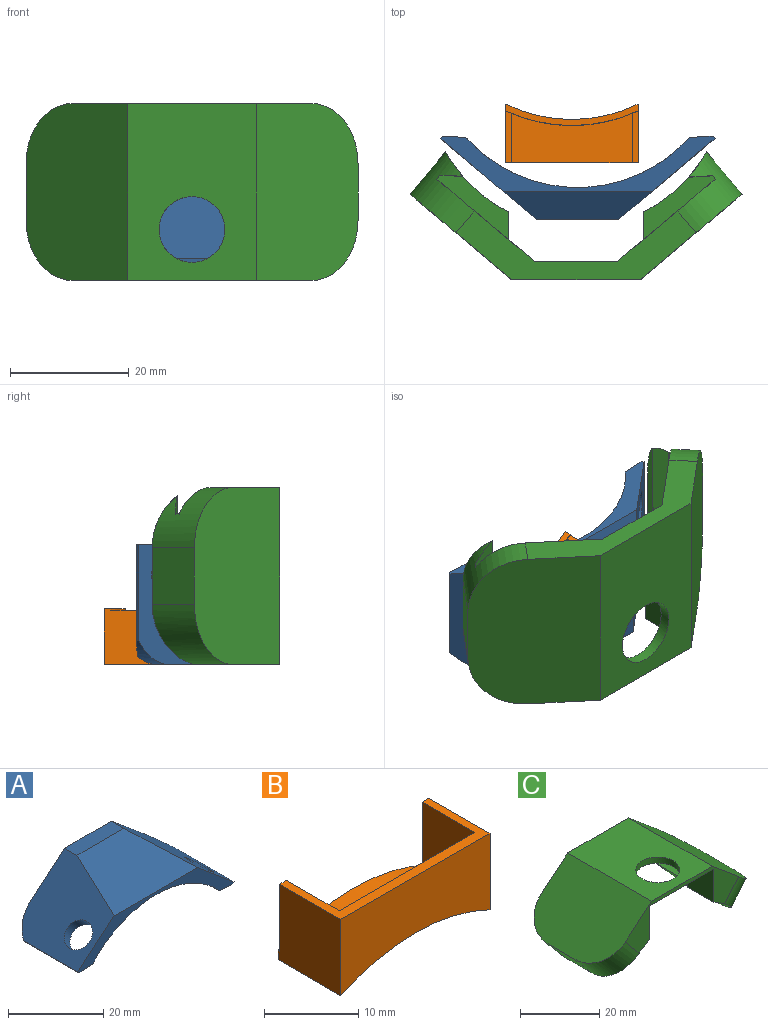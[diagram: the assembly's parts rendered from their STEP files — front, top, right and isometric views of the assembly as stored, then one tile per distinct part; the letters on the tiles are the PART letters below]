
ASSEMBLY  parts=3 mates=2
PART A: 40 faces, bbox 47.4x21.3x18 mm
  f0: torus R=15.15mm, axis (0,-1,0), area 22.5mm2, adj f1,f8,f11,f12
  f1: cylinder r=29.12mm len=5.11mm, axis (0,1,0), area 19.9mm2, adj f0,f9,f10,f20
  f2: bspline ~8.45x2.65mm, area 0.1mm2, adj f3,f37
  f3: plane 9.44x3.14mm, normal (-0.64,0,-0.77), area 6.4mm2, adj f2,f18,f37
  f4: plane 8.75x2.45mm, normal (-0.64,0,-0.77), area 6.4mm2, adj f15,f16,f18,f37
  f5: bspline ~8.68x3.45mm, area 0.1mm2, adj f6,f36
  f6: plane 9.44x3.14mm, normal (0.64,0,-0.77), area 6.4mm2, adj f5,f19,f36
  f7: plane 8.75x2.45mm, normal (0.64,0,-0.77), area 6.4mm2, adj f19,f21,f22,f36
  f8: bspline ~7.83x4.14mm, area 18.1mm2, adj f0,f9,f13,f28
  f9: cylinder r=5.08mm len=5.11mm, axis (0,1,0), area 22.2mm2, adj f1,f8,f20,f28
  f10: cylinder r=5.08mm len=5.11mm, axis (0,-1,0), area 22.2mm2, adj f1,f11,f20,f27
  f11: bspline ~9.36x4.49mm, area 18.1mm2, adj f0,f10,f14,f27
  f12: cone r=29.12mm half-angle=20.6deg, axis (0,1,0), area 46.9mm2, adj f0,f13,f14,f26
  f13: bspline ~10.91x6.7mm, area 23.3mm2, adj f8,f12,f25,f28
  f14: bspline ~9.02x6.04mm, area 23.3mm2, adj f11,f12,f24,f27
  f15: bspline ~8.01x3.09mm, area 0.8mm2, adj f4,f35,f37
  f16: bspline ~4.22x2.61mm, area 0.8mm2, adj f4,f35,f37
  f17: cylinder r=10.16mm len=8.09mm, axis (0.64,0,0.77), area 21.6mm2, adj f20,f33,f34,f35,f37
  f18: cylinder r=3.37mm len=6.87mm, axis (-0.64,0,-0.77), area 56.4mm2, adj f3,f4,f33,f37
  f19: cylinder r=3.37mm len=6.87mm, axis (0.64,0,-0.77), area 56.4mm2, adj f6,f7,f31,f36
  f20: plane 33.94x10.44mm, normal (0,1,0), area 112.9mm2, adj f1,f9,f10,f17,f23,f27,f28,f31
  f21: bspline ~8.01x3.09mm, area 0.8mm2, adj f7,f29,f36
  f22: bspline ~4.22x2.61mm, area 0.8mm2, adj f7,f29,f36
  f23: cylinder r=10.16mm len=8.09mm, axis (0.64,0,-0.77), area 21.6mm2, adj f20,f29,f30,f31,f36
  f24: bspline ~7.31x5.83mm, area 11.5mm2, adj f14,f26,f27,f38
  f25: bspline ~7.31x5.83mm, area 11.5mm2, adj f13,f26,f28,f38
  f26: torus R=39.28mm, axis (0,1,0), area 80.2mm2, adj f12,f24,f25,f38
  f27: cylinder r=13.97mm len=20.19mm, axis (0,1,0), area 93.4mm2, adj f10,f11,f14,f20,f24,f37,f38
  f28: cylinder r=13.97mm len=20.19mm, axis (0,1,0), area 93.4mm2, adj f8,f9,f13,f20,f25,f36,f38
  f29: plane 19.3x4.37mm, normal (0.06,0,-1), area 70mm2, adj f21,f22,f23,f30,f36,f38
  f30: plane 16.13x0.39mm, normal (-0.77,0,-0.64), area 8.2mm2, adj f23,f29,f31,f38
  f31: plane 20.19x16.23mm, normal (-0.64,0,0.77), area 323.6mm2, adj f19,f20,f23,f30,f32,f38,f39
  f32: plane 13.93x3.68mm, normal (0,0,1), area 51.3mm2, adj f20,f31,f33,f39
  f33: plane 20.19x16.23mm, normal (0.64,0,0.77), area 323.6mm2, adj f17,f18,f20,f32,f34,f38,f39
  f34: plane 16.13x0.39mm, normal (0.77,0,-0.64), area 8.2mm2, adj f17,f33,f35,f38
  f35: plane 19.3x4.37mm, normal (-0.06,0,-1), area 70mm2, adj f15,f16,f17,f34,f37,f38
  f36: cylinder r=25.31mm len=20.19mm, axis (0,1,0), area 150.7mm2, adj f5,f6,f7,f19,f20,f21,f22,f23
  f37: cylinder r=25.31mm len=20.19mm, axis (0,1,0), area 150.7mm2, adj f2,f3,f4,f15,f16,f17,f18,f20
  f38: plane 46.4x9.45mm, normal (0,-1,0), area 109.7mm2, adj f24,f25,f26,f27,f28,f29,f30,f31
  f39: plane 24.83x16.51mm, normal (0,-0.27,0.96), area 332mm2, adj f31,f32,f33,f38
PART B: 12 faces, bbox 22.4x9.4x9.9 mm
  f0: cylinder r=25.31mm len=22.35mm, axis (0,1,0), area 218.1mm2, adj f1,f7,f8,f11
  f1: plane 9.9x9.42mm, normal (1,0,0), area 91.1mm2, adj f0,f2,f8,f9,f10,f11
  f2: plane 8.78x1.02mm, normal (0,1,0), area 8.7mm2, adj f1,f3,f9,f10
  f3: plane 8.33x7.9mm, normal (-1,0,0), area 65.7mm2, adj f2,f4,f9,f10
  f4: plane 20.32x8.33mm, normal (0,1,0), area 141.3mm2, adj f3,f5,f9,f10
  f5: plane 8.33x7.9mm, normal (1,0,0), area 65.7mm2, adj f4,f6,f9,f10
  f6: plane 8.78x1.02mm, normal (0,1,0), area 8.7mm2, adj f5,f7,f9,f10
  f7: plane 9.9x9.42mm, normal (-1,0,0), area 91.1mm2, adj f0,f6,f8,f9,f10,f11
  f8: plane 22.35x9.9mm, normal (0,-1,0), area 182.2mm2, adj f0,f1,f7,f9
  f9: plane 22.35x9.17mm, normal (0,0,1), area 44.4mm2, adj f1,f2,f3,f4,f5,f6,f7,f8
  f10: cylinder r=26.33mm len=22.35mm, axis (0,1,0), area 170.6mm2, adj f1,f2,f3,f4,f5,f6,f7,f11
  f11: plane 22.35x3.62mm, normal (0,1,0), area 23.5mm2, adj f0,f1,f7,f10
PART C: 68 faces, bbox 57x30.9x22.6 mm
  f0: plane 5.64x1.52mm, normal (0,-1,0), area 7.6mm2, adj f2,f6,f8,f55,f57
  f1: plane 14.12x3.94mm, normal (0,0,-1), area 55.6mm2, adj f3,f19,f28,f59
  f2: plane 3.06x2.74mm, normal (0.64,0,-0.77), area 4.6mm2, adj f0,f15,f51,f57
  f3: plane 16.5x13.84mm, normal (0.64,0,-0.77), area 49mm2, adj f1,f17,f24,f28,f51,f57,f59
  f4: plane 3.06x2.74mm, normal (-0.64,0,-0.77), area 4.6mm2, adj f5,f7,f47,f58
  f5: cylinder r=10.29mm len=20.57mm, axis (-0.64,0,-0.77), area 223.3mm2, adj f4,f19,f20,f52,f53,f54,f58,f66
  f6: plane 7.9x0.7mm, normal (-1,0,0), area 5.5mm2, adj f0,f11,f55,f56
  f7: plane 5.64x1.52mm, normal (0,-1,0), area 7.6mm2, adj f4,f9,f10,f55,f58
  f8: plane 10.28x9.42mm, normal (1,0,0), area 96.9mm2, adj f0,f12,f14,f15,f55
  f9: plane 10.28x9.42mm, normal (-1,0,0), area 96.9mm2, adj f7,f13,f14,f47,f55
  f10: plane 7.9x0.7mm, normal (1,0,0), area 5.5mm2, adj f7,f11,f55,f56
  f11: plane 19.81x0.7mm, normal (0,-1,0), area 13.8mm2, adj f6,f10,f55,f56
  f12: cylinder r=25.31mm len=28.4mm, axis (0,1,0), area 145.3mm2, adj f8,f14,f15,f22,f23,f24,f27,f32
  f13: cylinder r=25.31mm len=28.49mm, axis (0,1,0), area 147.8mm2, adj f9,f14,f21,f25,f26,f34,f35,f36
  f14: plane 40.47x13.84mm, normal (0,-1,0), area 156.8mm2, adj f8,f9,f12,f13,f29,f30,f31,f45
  f15: plane 12.12x10.86mm, normal (0,1,0), area 41.5mm2, adj f2,f8,f12,f17,f18,f22,f49
  f16: plane 16.03x0.57mm, normal (-0.77,0,0.64), area 12mm2, adj f19,f20,f21,f25,f47,f54
  f17: plane 16.03x0.68mm, normal (0.77,0,0.64), area 14.3mm2, adj f3,f15,f18,f22,f24,f50
  f18: plane 5.26x3.69mm, normal (0.64,0,-0.77), area 9.6mm2, adj f15,f17,f51
  f19: plane 16.5x13.84mm, normal (-0.64,0,-0.77), area 49mm2, adj f1,f5,f16,f25,f28,f58,f59
  f20: plane 5.26x3.69mm, normal (-0.64,0,-0.77), area 9.6mm2, adj f5,f16,f47
  f21: plane 19.81x4.82mm, normal (0.06,0,1), area 72mm2, adj f13,f16,f25,f36,f47
  f22: plane 19.5x4.4mm, normal (-0.06,0,1), area 68.5mm2, adj f12,f15,f17,f23,f24
  f23: bspline ~7.34x1.85mm, area 0mm2, adj f12,f22
  f24: cylinder r=10.16mm len=13.78mm, axis (0.64,0,-0.77), area 108.3mm2, adj f3,f12,f17,f22,f27,f28,f29
  f25: cylinder r=10.16mm len=13.78mm, axis (0.64,0,0.77), area 108.9mm2, adj f13,f16,f19,f21,f26,f28,f31
  f26: plane 9.55x7.14mm, normal (0.77,0,-0.64), area 89mm2, adj f13,f25,f31,f46
  f27: plane 9.55x7.14mm, normal (-0.77,0,-0.64), area 89mm2, adj f12,f24,f29,f45
  f28: plane 40.47x11.59mm, normal (0,1,0), area 178.9mm2, adj f1,f3,f19,f24,f25,f29,f30,f31
  f29: plane 29.87x17.19mm, normal (-0.64,0,0.77), area 626mm2, adj f14,f24,f27,f28,f30,f45
  f30: plane 29.87x21.65mm, normal (0,0,1), area 549.7mm2, adj f14,f28,f29,f31,f60
  f31: plane 29.87x17.19mm, normal (0.64,0,0.77), area 626mm2, adj f14,f25,f26,f28,f30,f46
  f32: plane 9.44x3.14mm, normal (0.64,0,-0.77), area 6.4mm2, adj f12,f40,f43
  f33: plane 9.44x3.14mm, normal (0.64,0,-0.77), area 6.4mm2, adj f12,f39,f43
  f34: plane 9.44x3.14mm, normal (-0.64,0,-0.77), area 6.4mm2, adj f13,f38,f41
  f35: plane 9.44x3.14mm, normal (-0.64,0,-0.77), area 6.4mm2, adj f13,f37,f41
  f36: bspline ~7.34x1.85mm, area 0mm2, adj f13,f21
  f37: bspline ~8.68x3.09mm, area 0.1mm2, adj f13,f35
  f38: bspline ~8.45x2.65mm, area 0.1mm2, adj f13,f34
  f39: bspline ~8.68x3.45mm, area 0.1mm2, adj f12,f33
  f40: bspline ~8.45x2.3mm, area 0.1mm2, adj f12,f32
  f41: cylinder r=3.37mm len=7.03mm, axis (-0.64,0,-0.77), area 61.8mm2, adj f13,f34,f35,f42
  f42: plane 6.73x5.16mm, normal (-0.64,0,-0.77), area 35.6mm2, adj f41
  f43: cylinder r=3.37mm len=7.03mm, axis (0.64,0,-0.77), area 61.8mm2, adj f12,f32,f33,f44
  f44: plane 6.73x5.16mm, normal (0.64,0,-0.77), area 35.6mm2, adj f43
  f45: cylinder r=10.16mm len=13.78mm, axis (-0.64,0,0.77), area 136.3mm2, adj f12,f14,f27,f29
  f46: cylinder r=10.16mm len=13.78mm, axis (-0.64,0,-0.77), area 136.3mm2, adj f13,f14,f26,f31
  f47: plane 12.12x10.75mm, normal (0,1,0), area 41.1mm2, adj f4,f9,f13,f16,f20,f21,f53
  f48: plane 20.72x15.91mm, normal (0.64,0,-0.77), area 332.4mm2, adj f51,f63,f64
  f49: plane 7.22x6.06mm, normal (-0.64,0,0.77), area 7.3mm2, adj f15,f51
  f50: plane 7.77x0.58mm, normal (-0.64,0,0.77), area 4mm2, adj f17,f51
  f51: cylinder r=10.29mm len=20.57mm, axis (0.64,0,-0.77), area 223.7mm2, adj f2,f3,f18,f48,f49,f50,f57,f61
  f52: plane 20.71x15.89mm, normal (-0.64,0,-0.77), area 332.2mm2, adj f5,f65,f66,f67
  f53: plane 7.22x6.06mm, normal (0.64,0,0.77), area 7.3mm2, adj f5,f47
  f54: plane 7.77x0.58mm, normal (0.64,0,0.77), area 4mm2, adj f5,f16
  f55: plane 22.86x9.42mm, normal (0,0,-1), area 58.9mm2, adj f0,f6,f7,f8,f9,f10,f11,f14
  f56: plane 24.41x19.81mm, normal (0,0,-1), area 386.6mm2, adj f6,f10,f11,f57,f58,f59,f60
  f57: plane 16.51x3.66mm, normal (1,0,0), area 33.4mm2, adj f0,f2,f3,f51,f56,f59,f61
  f58: plane 16.51x3.66mm, normal (-1,0,0), area 33.4mm2, adj f4,f5,f7,f19,f56,f59,f66
  f59: plane 19.81x3.66mm, normal (0,-1,0), area 32mm2, adj f1,f3,f19,f56,f57,f58
  f60: cylinder r=5.56mm len=11.11mm, axis (0,0,-1), area 65.2mm2, adj f30,f56
  f61: cylinder r=0.64mm len=3.43mm, axis (1,0,0), area 10.1mm2, adj f51,f57,f62
  f62: plane 0.54x0.31mm, normal (1,0,0), area 0mm2, adj f51,f61
  f63: plane 0.55x0.06mm, normal (1,0,0), area 0mm2, adj f48,f64
  f64: cylinder r=0.64mm len=0.55mm, axis (1,0,0), area 0mm2, adj f48,f63
  f65: plane 0.98x0.23mm, normal (-1,0,0), area 0.2mm2, adj f52,f66,f67
  f66: cylinder r=0.64mm len=3.63mm, axis (-1,0,0), area 10.5mm2, adj f5,f52,f58,f65,f67
  f67: cylinder r=0.64mm len=0.49mm, axis (-1,0,0), area 0.1mm2, adj f52,f65,f66
PLACE A rot(axis=(0,-0.71,0.71),180deg) t=(-14.27,26.37,43.41)mm
PLACE B rot(axis=(1,0,0),90deg) t=(-15.24,37.86,1.6)mm
PLACE C rot(axis=(1,0,0),90deg) t=(-14.54,19.52,1.6)mm
MATE planar A.f20 <-> C.f14  axis (0,0,-1) through (-2.31,-0.08,7.57)mm
MATE planar B.f8 <-> C.f14  axis (0,0,-1) through (-15.24,9.36,7.57)mm
